# Revit family: 3D-AKE-00006970
name_source: partatom
category: Allgemeines Modell
units: mm (PartAtom-declared; Revit-internal decimal feet)

## family parameters
Arbeitsebenenbasiert = Nein
Beim Laden mit Abzugskörper schneiden = Nein
Bemaßung runder Anschluss = Durchmesser verwenden
Beschriftungsausrichtung beibehalten = Nein
Gemeinsam genutzt = Nein
Immer vertikal = Ja
Kann Basisbauteil für Bewehrung sein = Nein
Raumberechnungspunkt = Nein
Teiletyp = Normal

## types (1)
- Norm
    Abwicklungshöhe = 0
    Abwicklungslänge = 0
    Bauteilnummer = 3D-AKE-00006970
    Breite = 800
    DocNumber = 3D-AKE-00006970
    Entstanden aus = 3D-AKE-00006969.ipt
    Ersatzteilkennung = nein
    Erstellungsdatum = 14.04.2022
    Folder = Produkte\Standardzeichnungen\
    Genehmigungsdatum Konstr. = 14.04.2022
    Gewicht = 109,27 kg
    Höhe = 970
    Kennung = Standardteil
    Konstruktionsstatus = 1
    Revisionsnummer = -
    Tiefe = 747
    Titel = Green OS-80-55-Z
    VDS_Category = 3D-Konstruktion Bauteil
    Vorgabe-Ansicht = 0 mm  [stored 0 ft]

note: [stored X ft] marks values corroborated as IEEE doubles in the binary element streams (Revit-internal decimal feet)
